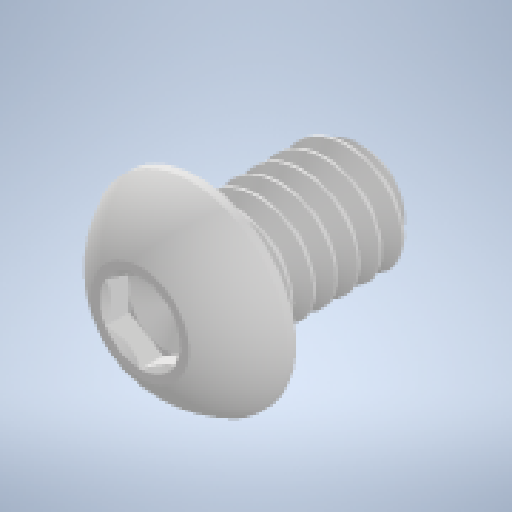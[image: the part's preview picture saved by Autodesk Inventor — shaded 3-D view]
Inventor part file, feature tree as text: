
AUTODESK INVENTOR PART (.ipt)
format: ipt  version: 2024 (Build 280153000, 153)  size: 467,968 bytes
history: native  units: in
note: dims shown in document units (in); Inventor stores cm internally (conversion verified against a paired STEP export)
features: revolve x1
ambient origin geometry x8: Origin, YZ Plane, XZ Plane, XY Plane, X Axis, Y Axis, Z Axis, Center Point
bodies: Solid1 (feature_tree)
feature tree (1):
  revolve  "Revolve2"  [1 undecoded]
note: 1 required parameter value undecoded (feature->parameter linkage not recoverable at this tier; creation-order binding heuristic only, values carry confidence <= 0.55)
